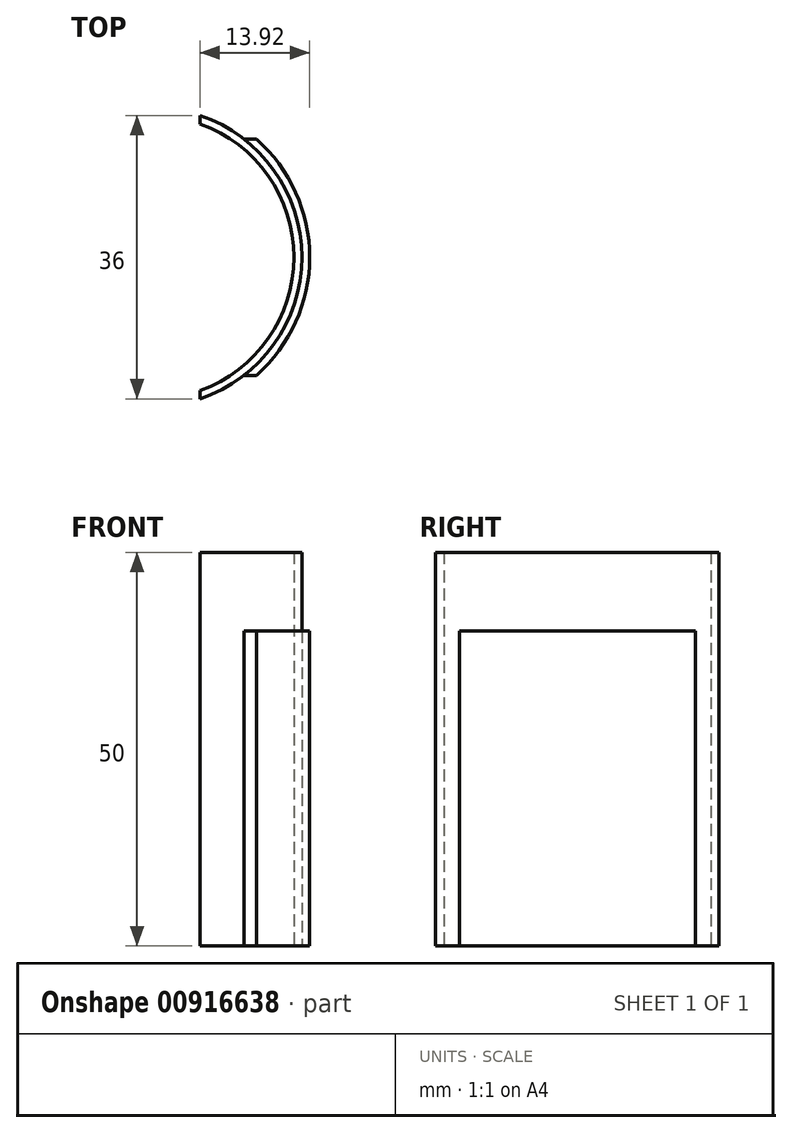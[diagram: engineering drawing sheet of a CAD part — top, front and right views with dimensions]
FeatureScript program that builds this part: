
annotation { "Feature Type Name" : "Feature", "Feature Type Description" : "" }
export const myFeature = defineFeature(function(context is Context, id is Id, definition is map)
    precondition{}
    {
        {
            var Q0;
            Q0=qCreatedBy(makeId("Top.planeOp"),FACE);
            var sketch = newSketch(context, id + "F0", { "sketchPlane" : qUnion([Q0])});
            skLineSegment(sketch, "E0", {"start": v(-31.27, 18) * mm, "end": v(35.9, 18) * mm, "construction": true});
            skLineSegment(sketch, "E1", {"start": v(-31.4, -18) * mm, "end": v(37.56, -18) * mm, "construction": true});
            skLineSegment(sketch, "E2", {"start": v(19, 24) * mm, "end": v(19, -23.45) * mm, "construction": true});
            skLineSegment(sketch, "E3", {"start": v(18, 21.16) * mm, "end": v(18, -24.4) * mm, "construction": true});
            skLineSegment(sketch, "E4", {"start": v(0, 18) * mm, "end": v(6.08, 18) * mm});
            skLineSegment(sketch, "E5", {"start": v(0, -18) * mm, "end": v(6.08, -18) * mm});
            skLineSegment(sketch, "E6", {"start": v(6.08, 18) * mm, "end": v(6.08, -18) * mm, "construction": true});
            skLineSegment(sketch, "E7", {"start": v(6.08, 18) * mm, "end": v(6.08, 16.94) * mm});
            skLineSegment(sketch, "E8", {"start": v(6.08, -18) * mm, "end": v(6.08, -16.94) * mm});
            skArc(sketch, "E9", {"start": v(19, 0) * mm, "mid": v(15.44, 11.08) * mm, "end": v(6.08, 18) * mm});
            skArc(sketch, "E10", {"start": v(19, 0) * mm, "mid": v(15.44, -11.08) * mm, "end": v(6.08, -18) * mm});
            skArc(sketch, "E11", {"start": v(18, 0) * mm, "mid": v(14.72, 10.36) * mm, "end": v(6.08, 16.94) * mm});
            skArc(sketch, "E12", {"start": v(18, 0) * mm, "mid": v(14.72, -10.36) * mm, "end": v(6.08, -16.94) * mm});
            skLineSegment(sketch, "E13", {"start": v(6.08, 16.94) * mm, "end": v(6.08, 18) * mm});
            skSolve(sketch);
        }
        {
            var Q0;
            Q0=qCreatedBy(makeId("Top.planeOp"),FACE);
            var sketch = newSketch(context, id + "F1", { "sketchPlane" : qUnion([Q0])});
            skLineSegment(sketch, "E14", {"start": v(-40.54, 15) * mm, "end": v(32.56, 15) * mm, "construction": true});
            skLineSegment(sketch, "E15", {"start": v(-40.83, -15) * mm, "end": v(35.75, -15) * mm, "construction": true});
            skLineSegment(sketch, "E16", {"start": v(19, 30.76) * mm, "end": v(19, -40.6) * mm, "construction": true});
            skLineSegment(sketch, "E17", {"start": v(20, 31.18) * mm, "end": v(20, -33.74) * mm, "construction": true});
            skArc(sketch, "E18", {"start": v(19, 0) * mm, "mid": v(17.07, 8.35) * mm, "end": v(11.66, 15) * mm});
            skArc(sketch, "E19", {"start": v(19, 0) * mm, "mid": v(17.07, -8.35) * mm, "end": v(11.66, -15) * mm});
            skArc(sketch, "E20", {"start": v(20, 0) * mm, "mid": v(18.23, 8.23) * mm, "end": v(13.23, 15) * mm});
            skArc(sketch, "E21", {"start": v(20, 0) * mm, "mid": v(18.23, -8.23) * mm, "end": v(13.23, -15) * mm});
            skLineSegment(sketch, "E22", {"start": v(11.66, 15) * mm, "end": v(13.23, 15) * mm});
            skLineSegment(sketch, "E23", {"start": v(11.66, -15) * mm, "end": v(13.23, -15) * mm});
            skSolve(sketch);
        }
        {
            var Q0;
            Q0=makeQuery(id+"F1.imprint","IMPRINT",FACE,{"disambiguationData":[TD([[makeQuery(id+"F1.imprint","IMPRINT",EDGE,{"derivedFrom":sQuery(id+"F1.wireOp",EDGE,"E18")}),-1.0]])]});
            extrude(context, id + "F2", {"entities" : qUnion([Q0]), "depth" : 40 * mm, "offsetDistance" : 25 * mm});
        }
        {
            var Q0;
            Q0=makeQuery(id+"F0.imprint","IMPRINT",FACE,{"disambiguationData":[TD([[makeQuery(id+"F0.imprint","IMPRINT",EDGE,{"derivedFrom":sQuery(id+"F0.wireOp",EDGE,"E9")}),1.0]])]});
            extrude(context, id + "F3", {"entities" : qUnion([Q0]), "depth" : 50 * mm, "offsetDistance" : 25 * mm});
        }
    });
